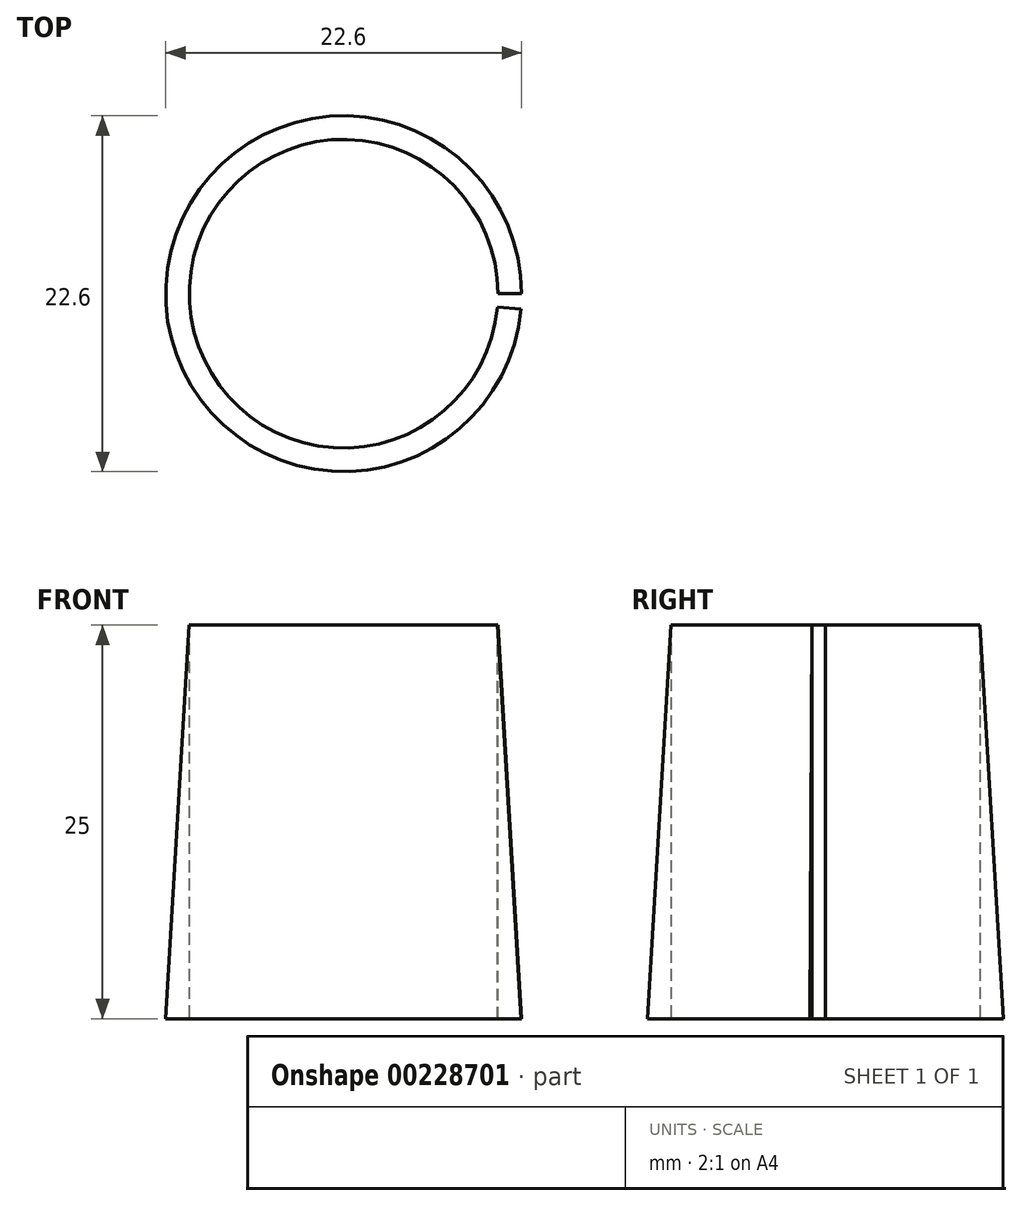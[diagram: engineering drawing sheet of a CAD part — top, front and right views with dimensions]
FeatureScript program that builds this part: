
annotation { "Feature Type Name" : "Feature", "Feature Type Description" : "" }
export const myFeature = defineFeature(function(context is Context, id is Id, definition is map)
    precondition{}
    {
        {
            var Q0;
            Q0=qCreatedBy(makeId("Front.planeOp"),FACE);
            var sketch = newSketch(context, id + "F0", { "sketchPlane" : qUnion([Q0])});
            skLineSegment(sketch, "E0", {"start": v(9.8, 0) * mm, "end": v(9.8, 25) * mm});
            skLineSegment(sketch, "E1", {"start": v(9.8, 25) * mm, "end": v(11.3, 0) * mm});
            skLineSegment(sketch, "E2", {"start": v(11.3, 0) * mm, "end": v(9.8, 0) * mm});
            skLineSegment(sketch, "E3", {"start": v(0, 0) * mm, "end": v(0, 29.7) * mm, "construction": true});
            skSolve(sketch);
        }
        {
            var Q0;
            Q0=makeQuery(id+"F0.imprint","IMPRINT",FACE,{"disambiguationData":[TD([[makeQuery(id+"F0.imprint","IMPRINT",EDGE,{"derivedFrom":sQuery(id+"F0.wireOp",EDGE,"E0")}),-1.0]])]});
            var Q1;
            Q1=sQuery(id+"F0.wireOp",EDGE,"E3");
            revolve(context, id + "F1", {"entities" : qUnion([Q0]), "axis" : qUnion([Q1]), "revolveType" : RevolveType.ONE_DIRECTION, "angle" : 355 * degree});
        }
    });
